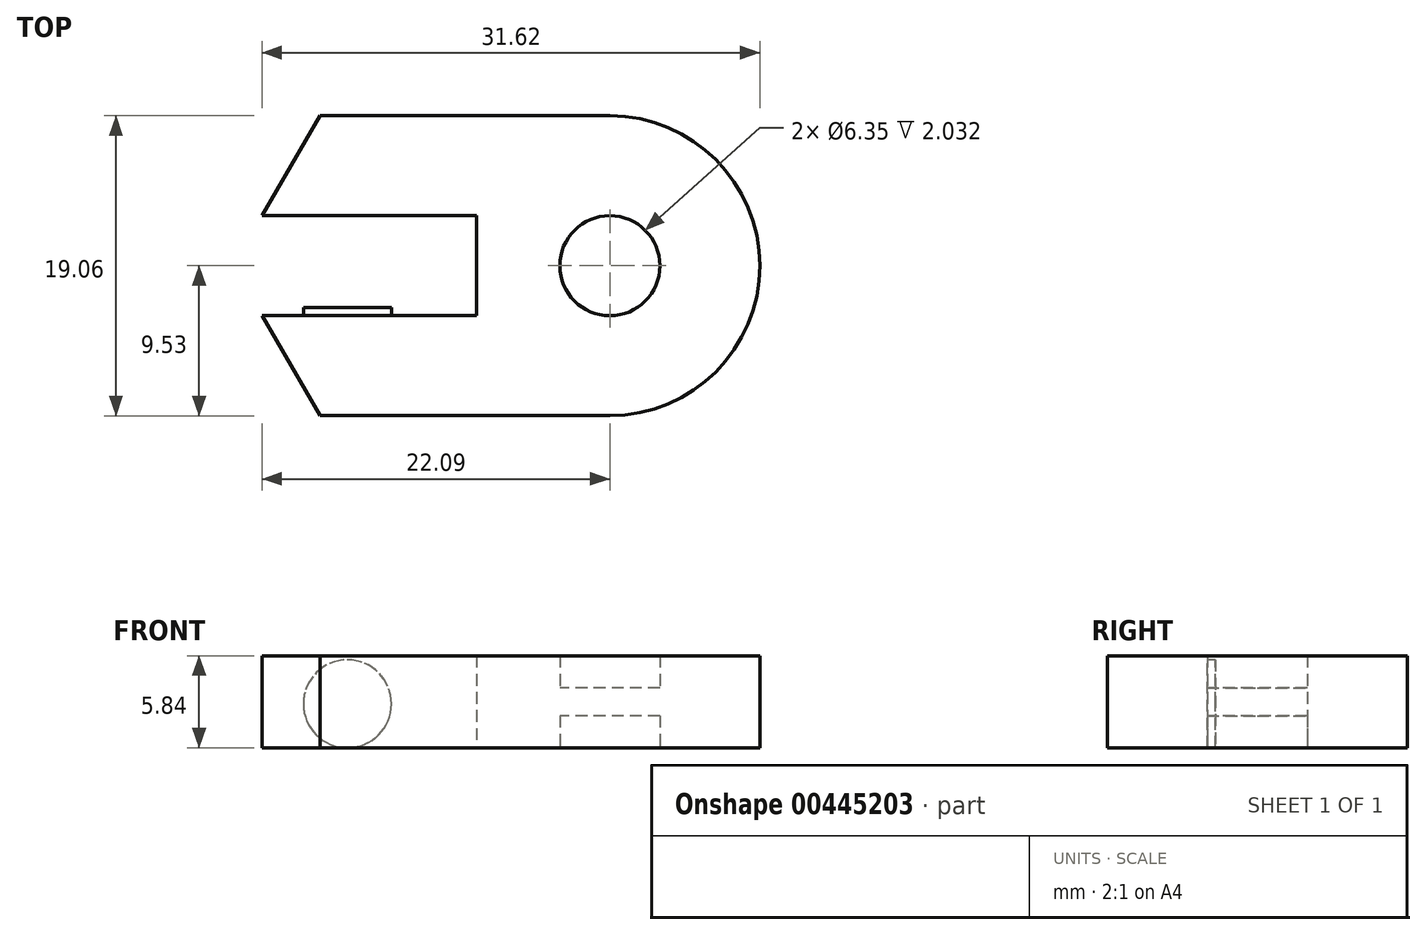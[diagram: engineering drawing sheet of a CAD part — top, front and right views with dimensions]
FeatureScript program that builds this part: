
annotation { "Feature Type Name" : "Feature", "Feature Type Description" : "" }
export const myFeature = defineFeature(function(context is Context, id is Id, definition is map)
    precondition{}
    {
        {
            var Q0;
            Q0=qCreatedBy(makeId("Top.planeOp"),FACE);
            var sketch = newSketch(context, id + "F0", { "sketchPlane" : qUnion([Q0])});
            skArc(sketch, "E0", {"start": v(-8.98, -3.17) * mm, "mid": v(9.52, 0) * mm, "end": v(-8.98, 3.17) * mm});
            skCircle(sketch, "E1", {"center": v(0, 0) * mm, "radius": 3.18 * mm});
            skPoint(sketch, "E2", {"position": v(-9.53, 0) * mm});
            skLineSegment(sketch, "E3", {"start": v(0, 9.53) * mm, "end": v(-9.53, 9.53) * mm});
            skLineSegment(sketch, "E4", {"start": v(-9.53, 9.53) * mm, "end": v(-12.06, 9.52) * mm});
            skLineSegment(sketch, "E5", {"start": v(0, -9.53) * mm, "end": v(-9.53, -9.53) * mm});
            skLineSegment(sketch, "E6", {"start": v(-9.53, -9.52) * mm, "end": v(-12.06, -9.52) * mm});
            skPoint(sketch, "E7.orphan", {"position": v(-22.65, 0) * mm});
            skLineSegment(sketch, "E8", {"start": v(-17.36, 0) * mm, "end": v(-8.47, 0) * mm});
            skPoint(sketch, "E8.endSnap0", {"position": v(-17.36, 0) * mm});
            skLineSegment(sketch, "E9", {"start": v(0, 0) * mm, "end": v(-8.47, 0) * mm});
            skPoint(sketch, "E10.start.orphan", {"position": v(-17.36, 4.76) * mm});
            skPoint(sketch, "E11.trimOffspring.end.orphan", {"position": v(-17.36, -4.76) * mm});
            skLineSegment(sketch, "E12", {"start": v(-12.06, 9.52) * mm, "end": v(-18.41, 9.52) * mm});
            skLineSegment(sketch, "E13", {"start": v(-22.08, 3.17) * mm, "end": v(-18.41, 9.52) * mm});
            skLineSegment(sketch, "E14", {"start": v(-22.09, -3.17) * mm, "end": v(-18.41, -9.53) * mm});
            skLineSegment(sketch, "E15", {"start": v(-18.41, -9.52) * mm, "end": v(-12.06, -9.52) * mm});
            skLineSegment(sketch, "E16", {"start": v(-22.08, 3.17) * mm, "end": v(-8.47, 3.17) * mm});
            skLineSegment(sketch, "E17", {"start": v(-8.47, 3.17) * mm, "end": v(-8.47, -3.17) * mm});
            skLineSegment(sketch, "E18", {"start": v(-8.47, -3.17) * mm, "end": v(-22.09, -3.17) * mm});
            skLineSegment(sketch, "E19", {"start": v(0, 0) * mm, "end": v(-16.67, 0) * mm});
            skLineSegment(sketch, "E20.trimOffspring", {"start": v(-17.36, 0) * mm, "end": v(-22.65, 0) * mm});
            skPoint(sketch, "E21", {"position": v(-16.67, 3.17) * mm});
            skPoint(sketch, "E22", {"position": v(-16.67, -3.17) * mm});
            skLineSegment(sketch, "E23.trimOffspring", {"start": v(-9.53, 0) * mm, "end": v(-16.67, 0) * mm});
            skSolve(sketch);
        }
        {
            var Q0;
            Q0 = qSketchRegion(id + "F0", true);
            extrude(context, id + "F1", {"entities" : qUnion([Q0]), "depth" : 5.84 * mm});
        }
        {
            var Q0;
            Q0=makeQuery(id+"F0.imprint","IMPRINT",FACE,{"disambiguationData":[TD([[makeQuery(id+"F0.imprint","IMPRINT",EDGE,{"derivedFrom":sQuery(id+"F0.wireOp",EDGE,"E1")}),1.0]])]});
            extrude(context, id + "F2", {"entities" : qUnion([Q0]), "operationType" : NewBodyOperationType.ADD, "depth" : 3.8 * mm});
        }
        {
            var Q0;
            Q0=makeQuery(id+"F0.imprint","IMPRINT",FACE,{"disambiguationData":[TD([[makeQuery(id+"F0.imprint","IMPRINT",EDGE,{"derivedFrom":sQuery(id+"F0.wireOp",EDGE,"E1")}),1.0]])]});
            extrude(context, id + "F3", {"entities" : qUnion([Q0]), "operationType" : NewBodyOperationType.REMOVE, "depth" : 2.03 * mm});
        }
        {
            var Q0;
            Q0=makeQuery(id+"F1.opExtrude","SWEPT_FACE",FACE,{"disambiguationData":[OSD([sQuery(id+"F0.wireOp",EDGE,"E18")])]});
            var sketch = newSketch(context, id + "F4", { "sketchPlane" : qUnion([Q0])});
            skLineSegment(sketch, "E24", {"start": v(16.67, 0) * mm, "end": v(16.67, 5.59) * mm});
            skCircle(sketch, "E25", {"center": v(16.67, 2.8) * mm, "radius": 2.8 * mm});
            skSolve(sketch);
        }
        {
            var Q0;
            {var subQ0=sQuery(id+"F4.wireOp",EDGE,"E24");Q0=makeQuery(id+"F4.imprint","IMPRINT",FACE,{"disambiguationData":[TD([[makeQuery(id+"F4.imprint","IMPRINT",EDGE,{"derivedFrom":subQ0}),1.0]])]});}
            var Q1;
            {var subQ0=sQuery(id+"F4.wireOp",EDGE,"E24");Q1=makeQuery(id+"F4.imprint","IMPRINT",FACE,{"disambiguationData":[TD([[makeQuery(id+"F4.imprint","IMPRINT",EDGE,{"derivedFrom":subQ0}),-1.0]])]});}
            extrude(context, id + "F5", {"entities" : qUnion([Q0, Q1]), "operationType" : NewBodyOperationType.ADD, "depth" : 0.5 * mm});
        }
    });
